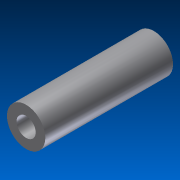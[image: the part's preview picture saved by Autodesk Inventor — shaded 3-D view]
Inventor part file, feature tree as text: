
AUTODESK INVENTOR PART (.ipt)
format: ipt  version: 2012 (Build 160160000, 160)  size: 79,872 bytes
history: native  units: in
note: dims shown in document units (in); Inventor stores cm internally (conversion verified against a paired STEP export)
features: extrude x1, sketch x1
ambient origin geometry x8: Origin, YZ Plane, XZ Plane, XY Plane, X Axis, Y Axis, Z Axis, Center Point
bodies: Solid1 (feature_tree)
feature tree (2):
  extrude  "Extrusion1"  Depth=0.2362in
  sketch  "Sketch1"  dims[d0=0.1181in d1=0.2362in d2=0.7874in d3=0.0in]
